# Revit family: GA-651LH
name_source: partatom
category: Plumbing Fixtures
revit_build: Autodesk Revit Architecture 2012 (Build: 20110309_2315(x64)
units: mm (PartAtom-declared; Revit-internal decimal feet)

## types (1)
- GA-651LH
    Aerator = C-M24X1
    Assembly Code = D2010
    CW Connection = Yes
    CWFU = 0
    Connection tubes = C-M10X1/2
    Cost = 0 $
    Default Elevation = 0' - 0"
    Description = Single lever with pop-up waste. 1/2"BSP female inlets
Single lever with pop-up waste. 1/2"BSP female inlets
    Gala looped handle = S-650/4
    HW Connection = Yes
    HWFU = 0
    Keynote = 1/2" female 400mm long flexible inlets
    Manufacturer = COBRA
    Material = Chrome - Polished
    Model = GA-650LH
    Raised cartridge = S-SE950-1-R
    Range = Gala looped handle
    Type Comments = SANS 1480
    URL = http://www.cobra.co.za
    Vent Connection = No
    WFU = 0
    Waste Connection = No

## geometry (parser evidence)
native form markers: Blend x2
no freeform markers — native parametric forms only
